# Revit family: 304_cc0dd35f6c3c4451b3d4bef709c488
name_source: partatom
category: Pipe Accessories
revit_build: Autodesk Revit 2018 (Build: 20170223_1515(x64)
units: mm (PartAtom-declared; Revit-internal decimal feet)

## family parameters
Always vertical = Yes
Cut with Voids When Loaded = No
Part Type = Valve - Breaks Into
Round Connector Dimension = Use Diameter
Shared = No
Work Plane-Based = No

## types (8) — shared parameters
Description = Cast iron automatic balancing valve PN16
H13 = 10 mm  [stored 0.0328084 ft]
H13__ve = -10 mm  [stored -0.0328084 ft]
L2D = 210 mm  [stored 0.688976 ft]
L2D_Min = 3048 mm  [stored 10 ft]
Manufacturer = VIR
QmdConnectorList = 301;D;302;D
R10 = 8 mm  [stored 0.0262467 ft]
R2 = 15 mm  [stored 0.0492126 ft]
URL = http://www.vironline.com
W11 = 15 mm  [stored 0.0492126 ft]
W2D = 100 mm  [stored 0.328084 ft]
magiPartTypeId = 304
magiProductFamilyId = cc0dd35f6c3c4451b3d4bef709c488

## per-type parameters (varying)
| type | D | H10 | H2 | L | L11 | L_2 | R | R1 | magiProductId |
| 9955 DN100 2 cartridges | 100 mm | 98 mm  [stored 0.321522 ft] | 87 mm | 210 mm  [stored 0.688976 ft] | 80 mm  [stored 0.262467 ft] | 105 mm  [stored 0.344488 ft] | 50 mm  [stored 0.164042 ft] | 82 mm | 25fb6f7bcf6d48258a76f078278433 |
| 9955 DN125 3 cartridges | 125 mm | 98 mm  [stored 0.321522 ft] | 102 mm | 210 mm  [stored 0.688976 ft] | 80 mm  [stored 0.262467 ft] | 105 mm  [stored 0.344488 ft] | 63 mm | 97 mm  [stored 0.318241 ft] | 307cb4ac79044b7b87fb3232c0f65e |
| 9955 DN150 4 cartridges | 150 mm | 97 mm  [stored 0.318241 ft] | 113 mm  [stored 0.370735 ft] | 210 mm  [stored 0.688976 ft] | 80 mm  [stored 0.262467 ft] | 105 mm  [stored 0.344488 ft] | 75 mm  [stored 0.246063 ft] | 108 mm  [stored 0.354331 ft] | d240dccd63a34cc49efcc2c6e3e85e |
| 9955 DN200 7 cartridges | 200 mm | 98 mm  [stored 0.321522 ft] | 141 mm | 210 mm  [stored 0.688976 ft] | 80 mm  [stored 0.262467 ft] | 105 mm  [stored 0.344488 ft] | 100 mm  [stored 0.328084 ft] | 136 mm | 5b3151a9f920425c88907fa312c4b6 |
| 9955 DN250 10 cartridges | 250 mm | 97 mm  [stored 0.318241 ft] | 169 mm  [stored 0.554462 ft] | 210 mm  [stored 0.688976 ft] | 80 mm  [stored 0.262467 ft] | 105 mm  [stored 0.344488 ft] | 125 mm  [stored 0.410105 ft] | 164 mm  [stored 0.538058 ft] | c21c97a931af4e2d951356661b910b |
| 9955 DN300 14 cartridges | 300 mm | 98 mm  [stored 0.321522 ft] | 197 mm | 210 mm  [stored 0.688976 ft] | 80 mm  [stored 0.262467 ft] | 105 mm  [stored 0.344488 ft] | 150 mm  [stored 0.492126 ft] | 192 mm | 55b5771a05cb47da940a25be55f11b |
| 9955 DN65 1 cartridge | 65 mm | 98 mm  [stored 0.321522 ft] | 65 mm  [stored 0.213255 ft] | 170 mm  [stored 0.557743 ft] | 65 mm  [stored 0.213255 ft] | 85 mm  [stored 0.278871 ft] | 33 mm | 60 mm  [stored 0.19685 ft] | c9d4ffb5ac8440ce925b6d1f60583b |
| 9955 DN80 1 cartridge | 80 mm | 98 mm  [stored 0.321522 ft] | 71 mm | 170 mm  [stored 0.557743 ft] | 65 mm  [stored 0.213255 ft] | 85 mm  [stored 0.278871 ft] | 40 mm  [stored 0.131234 ft] | 66 mm | a046fd7616064abc87341f048f6c13 |

note: column(s) folded — value = type name in every type: MC Product Code

note: [stored X ft] marks values corroborated as IEEE doubles in the binary element streams (Revit-internal decimal feet)
